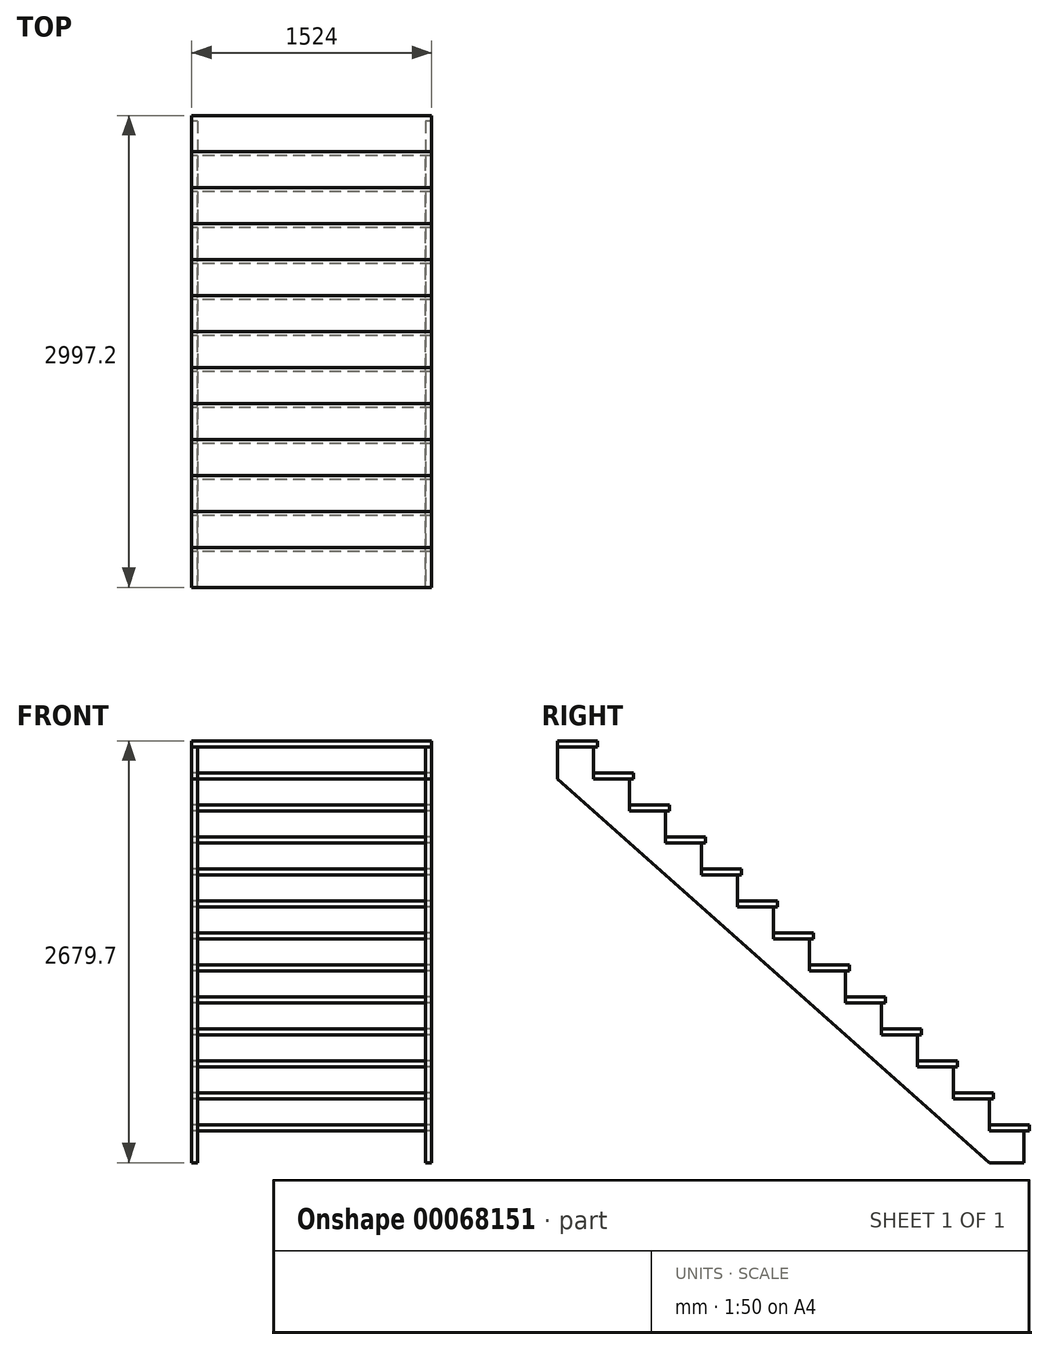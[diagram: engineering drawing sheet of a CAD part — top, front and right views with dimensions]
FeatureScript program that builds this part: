
annotation { "Feature Type Name" : "Feature", "Feature Type Description" : "" }
export const myFeature = defineFeature(function(context is Context, id is Id, definition is map)
    precondition{}
    {
        {
            var Q0;
            Q0=qCreatedBy(makeId("Right.planeOp"),FACE);
            var sketch = newSketch(context, id + "F0", { "sketchPlane" : qUnion([Q0])});
            skLineSegment(sketch, "E0.bottom", {"start": v(0, 0) * mm, "end": v(-254, 0) * mm});
            skLineSegment(sketch, "E0.top", {"start": v(0, 38.1) * mm, "end": v(-254, 38.1) * mm});
            skLineSegment(sketch, "E0.left", {"start": v(0, 0) * mm, "end": v(0, 38.1) * mm});
            skLineSegment(sketch, "E0.right", {"start": v(-254, 0) * mm, "end": v(-254, 38.1) * mm});
            skLineSegment(sketch, "E1.1.1.0", {"start": v(-482.6, 203.2) * mm, "end": v(-482.6, 241.3) * mm});
            skLineSegment(sketch, "E1.1.1.1", {"start": v(-228.6, 203.2) * mm, "end": v(-228.6, 241.3) * mm});
            skLineSegment(sketch, "E1.1.1.2", {"start": v(-228.6, 241.3) * mm, "end": v(-482.6, 241.3) * mm});
            skLineSegment(sketch, "E1.1.1.3", {"start": v(-228.6, 203.2) * mm, "end": v(-482.6, 203.2) * mm});
            skLineSegment(sketch, "E1.1.2.0", {"start": v(-457.2, 406.4) * mm, "end": v(-457.2, 444.5) * mm});
            skLineSegment(sketch, "E1.2.2.0", {"start": v(-711.2, 406.4) * mm, "end": v(-711.2, 444.5) * mm});
            skLineSegment(sketch, "E1.2.2.2", {"start": v(-457.2, 444.5) * mm, "end": v(-711.2, 444.5) * mm});
            skLineSegment(sketch, "E1.2.2.3", {"start": v(-457.2, 406.4) * mm, "end": v(-711.2, 406.4) * mm});
            skLineSegment(sketch, "E1.3.3.0", {"start": v(-939.8, 609.6) * mm, "end": v(-939.8, 647.7) * mm});
            skLineSegment(sketch, "E1.3.3.1", {"start": v(-685.8, 609.6) * mm, "end": v(-685.8, 647.7) * mm});
            skLineSegment(sketch, "E1.3.3.2", {"start": v(-685.8, 647.7) * mm, "end": v(-939.8, 647.7) * mm});
            skLineSegment(sketch, "E1.3.3.3", {"start": v(-685.8, 609.6) * mm, "end": v(-939.8, 609.6) * mm});
            skLineSegment(sketch, "E1.4.4.0", {"start": v(-1168.4, 812.8) * mm, "end": v(-1168.4, 850.9) * mm});
            skLineSegment(sketch, "E1.4.4.1", {"start": v(-914.4, 812.8) * mm, "end": v(-914.4, 850.9) * mm});
            skLineSegment(sketch, "E1.4.4.2", {"start": v(-914.4, 850.9) * mm, "end": v(-1168.4, 850.9) * mm});
            skLineSegment(sketch, "E1.4.4.3", {"start": v(-914.4, 812.8) * mm, "end": v(-1168.4, 812.8) * mm});
            skLineSegment(sketch, "E1.5.5.0", {"start": v(-1397, 1016) * mm, "end": v(-1397, 1054.1) * mm});
            skLineSegment(sketch, "E1.5.5.1", {"start": v(-1143, 1016) * mm, "end": v(-1143, 1054.1) * mm});
            skLineSegment(sketch, "E1.5.5.2", {"start": v(-1143, 1054.1) * mm, "end": v(-1397, 1054.1) * mm});
            skLineSegment(sketch, "E1.5.5.3", {"start": v(-1143, 1016) * mm, "end": v(-1397, 1016) * mm});
            skLineSegment(sketch, "E1.6.6.0", {"start": v(-1625.6, 1219.2) * mm, "end": v(-1625.6, 1257.3) * mm});
            skLineSegment(sketch, "E1.6.6.1", {"start": v(-1371.6, 1219.2) * mm, "end": v(-1371.6, 1257.3) * mm});
            skLineSegment(sketch, "E1.6.6.2", {"start": v(-1371.6, 1257.3) * mm, "end": v(-1625.6, 1257.3) * mm});
            skLineSegment(sketch, "E1.6.6.3", {"start": v(-1371.6, 1219.2) * mm, "end": v(-1625.6, 1219.2) * mm});
            skLineSegment(sketch, "E1.7.7.0", {"start": v(-1854.2, 1422.4) * mm, "end": v(-1854.2, 1460.5) * mm});
            skLineSegment(sketch, "E1.7.7.1", {"start": v(-1600.2, 1422.4) * mm, "end": v(-1600.2, 1460.5) * mm});
            skLineSegment(sketch, "E1.7.7.2", {"start": v(-1600.2, 1460.5) * mm, "end": v(-1854.2, 1460.5) * mm});
            skLineSegment(sketch, "E1.7.7.3", {"start": v(-1600.2, 1422.4) * mm, "end": v(-1854.2, 1422.4) * mm});
            skLineSegment(sketch, "E1.8.8.0", {"start": v(-2082.8, 1625.6) * mm, "end": v(-2082.8, 1663.7) * mm});
            skLineSegment(sketch, "E1.8.8.1", {"start": v(-1828.8, 1625.6) * mm, "end": v(-1828.8, 1663.7) * mm});
            skLineSegment(sketch, "E1.8.8.2", {"start": v(-1828.8, 1663.7) * mm, "end": v(-2082.8, 1663.7) * mm});
            skLineSegment(sketch, "E1.8.8.3", {"start": v(-1828.8, 1625.6) * mm, "end": v(-2082.8, 1625.6) * mm});
            skLineSegment(sketch, "E1.8.9.0", {"start": v(-2057.4, 1828.8) * mm, "end": v(-2057.4, 1866.9) * mm});
            skLineSegment(sketch, "E1.9.9.0", {"start": v(-2311.4, 1828.8) * mm, "end": v(-2311.4, 1866.9) * mm});
            skLineSegment(sketch, "E1.9.9.2", {"start": v(-2057.4, 1866.9) * mm, "end": v(-2311.4, 1866.9) * mm});
            skLineSegment(sketch, "E1.9.9.3", {"start": v(-2057.4, 1828.8) * mm, "end": v(-2311.4, 1828.8) * mm});
            skLineSegment(sketch, "E2", {"start": v(362.42, -165.1) * mm, "end": v(-3419.6, -165.1) * mm, "construction": true});
            skLineSegment(sketch, "E3.1.1.0", {"start": v(-2286, 2032) * mm, "end": v(-2540, 2032) * mm});
            skLineSegment(sketch, "E3.1.1.1", {"start": v(-2286, 2070.1) * mm, "end": v(-2540, 2070.1) * mm});
            skLineSegment(sketch, "E3.1.1.2", {"start": v(-2540, 2032) * mm, "end": v(-2540, 2070.1) * mm});
            skLineSegment(sketch, "E3.1.1.3", {"start": v(-2540, 2032) * mm, "end": v(-2540, 2070.1) * mm});
            skLineSegment(sketch, "E3.1.1.4", {"start": v(-2286, 2032) * mm, "end": v(-2286, 2070.1) * mm});
            skLineSegment(sketch, "E3.2.2.0", {"start": v(-2514.6, 2235.2) * mm, "end": v(-2768.6, 2235.2) * mm});
            skLineSegment(sketch, "E3.2.2.1", {"start": v(-2514.6, 2273.3) * mm, "end": v(-2768.6, 2273.3) * mm});
            skLineSegment(sketch, "E3.2.2.2", {"start": v(-2768.6, 2235.2) * mm, "end": v(-2768.6, 2273.3) * mm});
            skLineSegment(sketch, "E3.2.2.4", {"start": v(-2514.6, 2235.2) * mm, "end": v(-2514.6, 2273.3) * mm});
            skLineSegment(sketch, "E3.3.3.0", {"start": v(-2743.2, 2438.4) * mm, "end": v(-2997.2, 2438.4) * mm});
            skLineSegment(sketch, "E3.3.3.1", {"start": v(-2743.2, 2476.5) * mm, "end": v(-2997.2, 2476.5) * mm});
            skLineSegment(sketch, "E3.3.3.2", {"start": v(-2997.2, 2438.4) * mm, "end": v(-2997.2, 2476.5) * mm});
            skLineSegment(sketch, "E3.3.3.4", {"start": v(-2743.2, 2438.4) * mm, "end": v(-2743.2, 2476.5) * mm});
            skLineSegment(sketch, "E4", {"start": v(-5548.04, 2476.5) * mm, "end": v(-1024, 2476.5) * mm, "construction": true});
            skSolve(sketch);
        }
        {
            var Q0;
            Q0 = qSketchRegion(id + "F0", true);
            extrude(context, id + "F1", {"entities" : qUnion([Q0]), "depth" : 1524 * mm});
        }
        {
            var Q0;
            Q0=qCreatedBy(makeId("Right.planeOp"),FACE);
            var sketch = newSketch(context, id + "F2", { "sketchPlane" : qUnion([Q0])});
            skLineSegment(sketch, "E5.1", {"start": v(-254, 0) * mm, "end": v(-254, 203.2) * mm});
            skLineSegment(sketch, "E5.2", {"start": v(-37.51, 0) * mm, "end": v(-254, 0) * mm});
            skLineSegment(sketch, "E5.3", {"start": v(-254, 203.2) * mm, "end": v(-482.6, 203.2) * mm});
            skLineSegment(sketch, "E5.4", {"start": v(-482.6, 203.2) * mm, "end": v(-482.6, 406.4) * mm});
            skLineSegment(sketch, "E6.0", {"start": v(-482.6, 406.4) * mm, "end": v(-711.2, 406.4) * mm});
            skLineSegment(sketch, "E6.1", {"start": v(-711.2, 406.4) * mm, "end": v(-711.2, 609.6) * mm});
            skLineSegment(sketch, "E6.2", {"start": v(-711.2, 609.6) * mm, "end": v(-939.8, 609.6) * mm});
            skLineSegment(sketch, "E6.3", {"start": v(-939.8, 609.6) * mm, "end": v(-939.8, 812.8) * mm});
            skLineSegment(sketch, "E6.4", {"start": v(-939.8, 812.8) * mm, "end": v(-1168.4, 812.8) * mm});
            skLineSegment(sketch, "E6.5", {"start": v(-1168.4, 812.8) * mm, "end": v(-1168.4, 1016) * mm});
            skLineSegment(sketch, "E6.6", {"start": v(-1168.4, 1016) * mm, "end": v(-1397, 1016) * mm});
            skLineSegment(sketch, "E6.7", {"start": v(-1397, 1016) * mm, "end": v(-1397, 1219.2) * mm});
            skLineSegment(sketch, "E6.8", {"start": v(-1397, 1219.2) * mm, "end": v(-1625.6, 1219.2) * mm});
            skLineSegment(sketch, "E6.9", {"start": v(-1625.6, 1219.2) * mm, "end": v(-1625.6, 1422.4) * mm});
            skLineSegment(sketch, "E6.10", {"start": v(-1625.6, 1422.4) * mm, "end": v(-1854.2, 1422.4) * mm});
            skLineSegment(sketch, "E6.11", {"start": v(-1854.2, 1422.4) * mm, "end": v(-1854.2, 1625.6) * mm});
            skLineSegment(sketch, "E6.12", {"start": v(-1854.2, 1625.6) * mm, "end": v(-2082.8, 1625.6) * mm});
            skLineSegment(sketch, "E6.13", {"start": v(-2082.8, 1625.6) * mm, "end": v(-2082.8, 1828.8) * mm});
            skLineSegment(sketch, "E6.14", {"start": v(-2057.4, 1828.8) * mm, "end": v(-2311.4, 1828.8) * mm});
            skLineSegment(sketch, "E6.15", {"start": v(-2311.4, 1828.8) * mm, "end": v(-2311.4, 2032) * mm});
            skLineSegment(sketch, "E6.16", {"start": v(-2311.4, 2032) * mm, "end": v(-2540, 2032) * mm});
            skLineSegment(sketch, "E6.17", {"start": v(-2540, 2032) * mm, "end": v(-2540, 2235.2) * mm});
            skLineSegment(sketch, "E6.18", {"start": v(-2540, 2235.2) * mm, "end": v(-2768.6, 2235.2) * mm});
            skLineSegment(sketch, "E6.19", {"start": v(-2768.6, 2235.2) * mm, "end": v(-2768.6, 2438.4) * mm});
            skLineSegment(sketch, "E6.20", {"start": v(-2768.6, 2438.4) * mm, "end": v(-2997.2, 2438.4) * mm});
            skPoint(sketch, "E7.orphan", {"position": v(-254, 38.1) * mm});
            skLineSegment(sketch, "E8", {"start": v(-37.51, 0) * mm, "end": v(-37.51, -203.2) * mm});
            skLineSegment(sketch, "E9", {"start": v(-37.51, -203.2) * mm, "end": v(-255.58, -203.2) * mm});
            skPoint(sketch, "E10.orphan", {"position": v(0, 0) * mm});
            skPoint(sketch, "E11.orphan", {"position": v(-228.6, 203.2) * mm});
            skLineSegment(sketch, "E12", {"start": v(-254, 203.2) * mm, "end": v(-456.5, -24.61) * mm, "construction": true});
            skLineSegment(sketch, "E13", {"start": v(-482.6, 203.2) * mm, "end": v(-254, 0) * mm, "construction": true});
            skLineSegment(sketch, "E14", {"start": v(-2997.2, 2233.8) * mm, "end": v(-255.58, -203.2) * mm});
            skPoint(sketch, "E15.orphan", {"position": v(-482.6, 241.3) * mm});
            skPoint(sketch, "E16.orphan", {"position": v(-457.2, 406.4) * mm});
            skPoint(sketch, "E17.orphan", {"position": v(-711.2, 444.5) * mm});
            skPoint(sketch, "E18.orphan", {"position": v(-685.8, 609.6) * mm});
            skPoint(sketch, "E19.orphan", {"position": v(-939.8, 647.7) * mm});
            skPoint(sketch, "E20.orphan", {"position": v(-914.4, 812.8) * mm});
            skPoint(sketch, "E21.orphan", {"position": v(-1168.4, 850.9) * mm});
            skPoint(sketch, "E22.orphan", {"position": v(-1143, 1016) * mm});
            skPoint(sketch, "E23.orphan", {"position": v(-1397, 1054.1) * mm});
            skPoint(sketch, "E24.orphan", {"position": v(-1371.6, 1219.2) * mm});
            skPoint(sketch, "E25.orphan", {"position": v(-1625.6, 1257.3) * mm});
            skPoint(sketch, "E26.orphan", {"position": v(-1600.2, 1422.4) * mm});
            skPoint(sketch, "E27.orphan", {"position": v(-1854.2, 1460.5) * mm});
            skPoint(sketch, "E28.orphan", {"position": v(-1828.8, 1625.6) * mm});
            skPoint(sketch, "E29.orphan", {"position": v(-2082.8, 1663.7) * mm});
            skPoint(sketch, "E30.orphan", {"position": v(-2311.4, 1866.9) * mm});
            skPoint(sketch, "E31.orphan", {"position": v(-2286, 2032) * mm});
            skPoint(sketch, "E32.orphan", {"position": v(-2540, 2070.1) * mm});
            skPoint(sketch, "E33.orphan", {"position": v(-2514.6, 2235.2) * mm});
            skPoint(sketch, "E34.orphan", {"position": v(-2768.6, 2273.3) * mm});
            skPoint(sketch, "E35.orphan", {"position": v(-2743.2, 2438.4) * mm});
            skLineSegment(sketch, "E36", {"start": v(-2997.2, 2438.4) * mm, "end": v(-2997.2, 2233.8) * mm});
            skSolve(sketch);
        }
        {
            var Q0;
            Q0 = qSketchRegion(id + "F2", true);
            extrude(context, id + "F3", {"entities" : qUnion([Q0]), "depth" : 38.1 * mm});
        }
        {
            var Q0;
            Q0=makeQuery(id+"F3.opExtrude","SWEPT_BODY",BODY,{"disambiguationData":[OSD([sQuery(id+"F2.wireOp",EDGE,"E5.1"),sQuery(id+"F2.wireOp",EDGE,"E5.2"),sQuery(id+"F2.wireOp",EDGE,"E5.3"),sQuery(id+"F2.wireOp",EDGE,"E5.4"),sQuery(id+"F2.wireOp",EDGE,"E6.0"),sQuery(id+"F2.wireOp",EDGE,"E6.1"),sQuery(id+"F2.wireOp",EDGE,"E6.2"),sQuery(id+"F2.wireOp",EDGE,"E6.3"),sQuery(id+"F2.wireOp",EDGE,"E6.4"),sQuery(id+"F2.wireOp",EDGE,"E6.5"),sQuery(id+"F2.wireOp",EDGE,"E6.6"),sQuery(id+"F2.wireOp",EDGE,"E6.7"),sQuery(id+"F2.wireOp",EDGE,"E6.8"),sQuery(id+"F2.wireOp",EDGE,"E6.9"),sQuery(id+"F2.wireOp",EDGE,"E6.10"),sQuery(id+"F2.wireOp",EDGE,"E6.11"),sQuery(id+"F2.wireOp",EDGE,"E6.12"),sQuery(id+"F2.wireOp",EDGE,"E6.13"),sQuery(id+"F2.wireOp",EDGE,"E6.14"),sQuery(id+"F2.wireOp",EDGE,"E6.15"),sQuery(id+"F2.wireOp",EDGE,"E6.16"),sQuery(id+"F2.wireOp",EDGE,"E6.17"),sQuery(id+"F2.wireOp",EDGE,"E6.18"),sQuery(id+"F2.wireOp",EDGE,"E6.19"),sQuery(id+"F2.wireOp",EDGE,"E6.20"),sQuery(id+"F2.wireOp",EDGE,"E8"),sQuery(id+"F2.wireOp",EDGE,"E9"),sQuery(id+"F2.wireOp",EDGE,"E14"),sQuery(id+"F2.wireOp",EDGE,"E36")])]});
            transform(context, id + "F4", {"entities" : qUnion([Q0]), "transformType" : TransformType.TRANSLATION_3D, "dx" : 1485.9 * mm, "dy" : 0 * mm, "dz" : 0 * mm, "makeCopy" : true});
        }
    });
